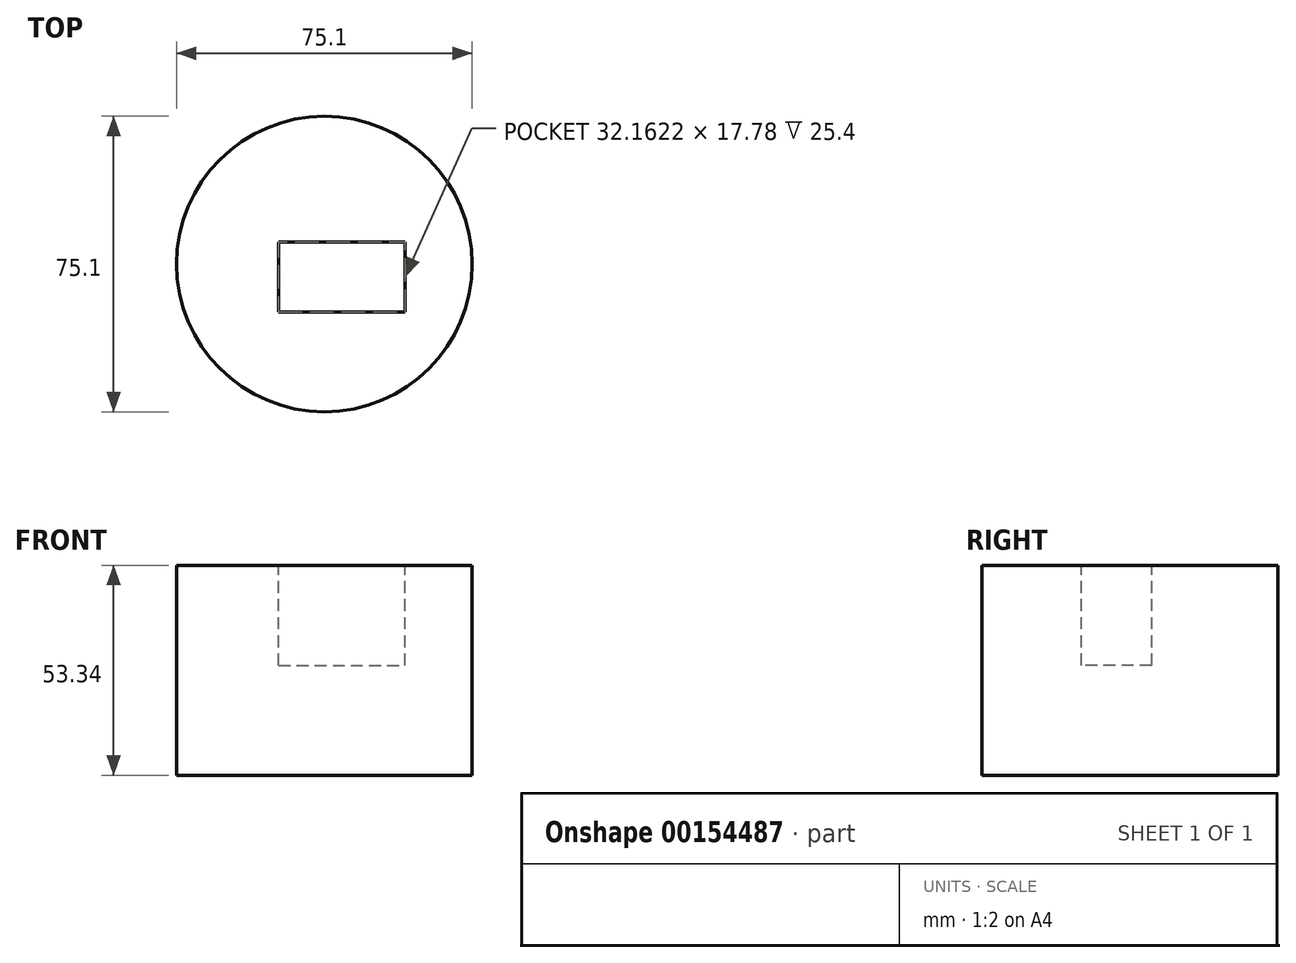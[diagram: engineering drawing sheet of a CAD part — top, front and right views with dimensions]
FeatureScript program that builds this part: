
annotation { "Feature Type Name" : "Feature", "Feature Type Description" : "" }
export const myFeature = defineFeature(function(context is Context, id is Id, definition is map)
    precondition{}
    {
        {
            var Q0;
            Q0=qCreatedBy(makeId("Top.planeOp"),FACE);
            var sketch = newSketch(context, id + "F0", { "sketchPlane" : qUnion([Q0])});
            skCircle(sketch, "E0", {"center": v(0, 0) * mm, "radius": 37.55 * mm});
            skSolve(sketch);
        }
        {
            var Q0;
            Q0 = qSketchRegion(id + "F0", true);
            extrude(context, id + "F1", {"entities" : qUnion([Q0]), "depth" : 53.34 * mm});
        }
        {
            var Q0;
            Q0=makeQuery(id+"F1.opExtrude","CAP_FACE",FACE,{"disambiguationData":[OSD([sQuery(id+"F0.wireOp",EDGE,"E0")])],"isStart":false});
            var sketch = newSketch(context, id + "F2", { "sketchPlane" : qUnion([Q0])});
            skLineSegment(sketch, "E1.bottom", {"start": v(-11.64, 5.55) * mm, "end": v(20.52, 5.55) * mm});
            skLineSegment(sketch, "E1.top", {"start": v(-11.64, -12.23) * mm, "end": v(20.52, -12.23) * mm});
            skLineSegment(sketch, "E1.left", {"start": v(-11.64, 5.55) * mm, "end": v(-11.64, -12.23) * mm});
            skLineSegment(sketch, "E1.right", {"start": v(20.52, 5.55) * mm, "end": v(20.52, -12.23) * mm});
            skSolve(sketch);
        }
        {
            var Q0;
            Q0 = qSketchRegion(id + "F2", true);
            extrude(context, id + "F3", {"entities" : qUnion([Q0]), "operationType" : NewBodyOperationType.REMOVE, "oppositeDirection" : true, "depth" : 25.4 * mm});
        }
    });
